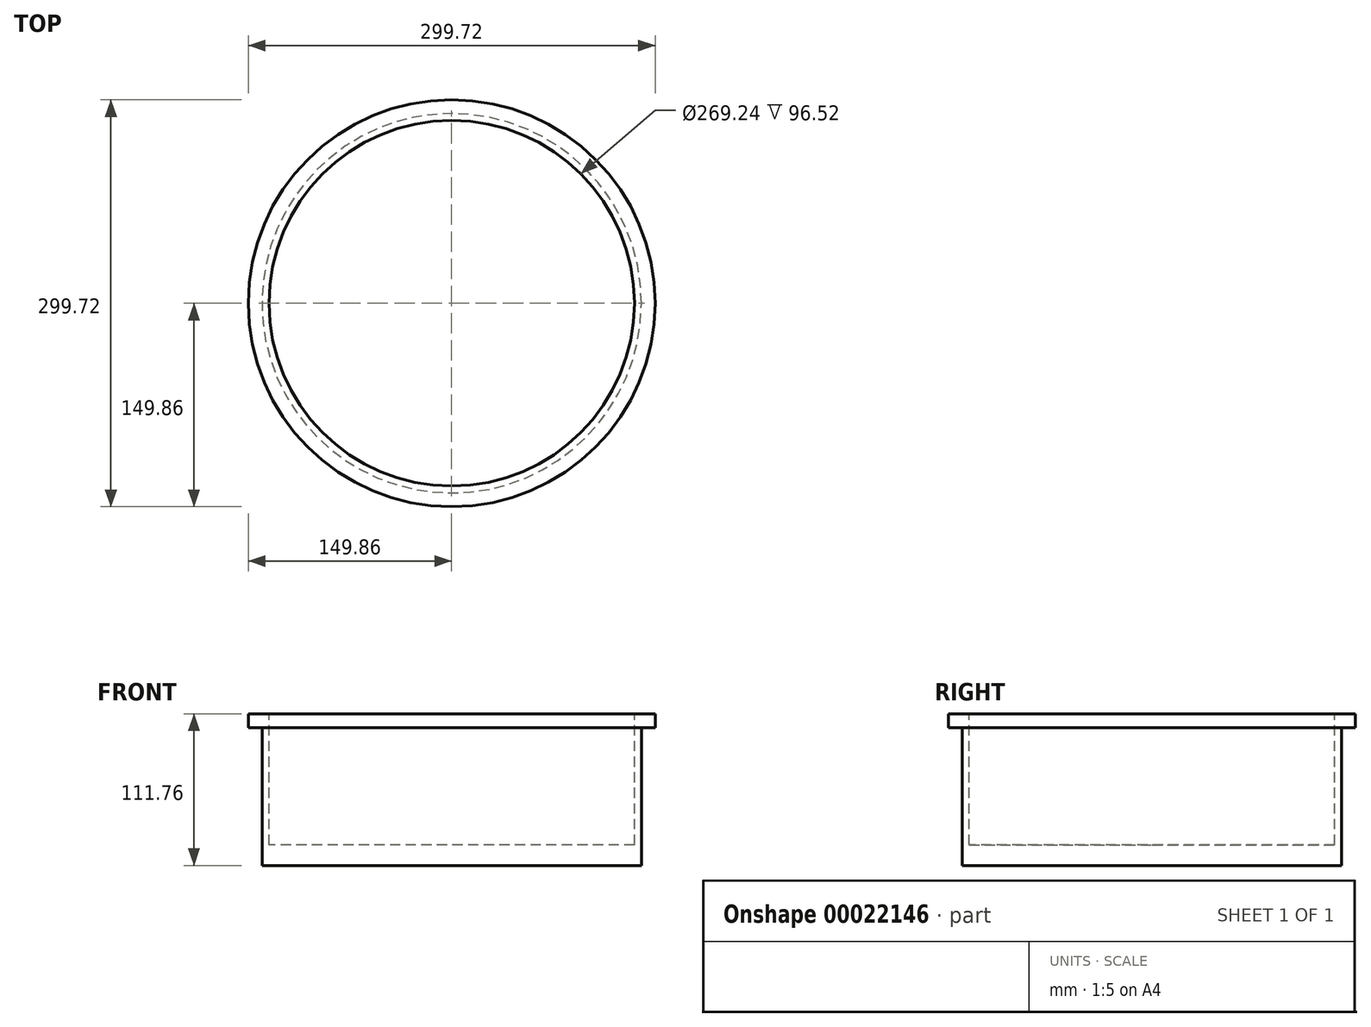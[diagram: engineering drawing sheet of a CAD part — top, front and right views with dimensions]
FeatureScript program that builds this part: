
annotation { "Feature Type Name" : "Feature", "Feature Type Description" : "" }
export const myFeature = defineFeature(function(context is Context, id is Id, definition is map)
    precondition{}
    {
        {
            var Q0;
            Q0=qCreatedBy(makeId("Front.planeOp"),FACE);
            var sketch = newSketch(context, id + "F0", { "sketchPlane" : qUnion([Q0])});
            skLineSegment(sketch, "E0.rect.bottom", {"start": v(149.86, 55.88) * mm, "end": v(0, 55.88) * mm});
            skLineSegment(sketch, "E0.rect.top", {"start": v(149.86, -55.88) * mm, "end": v(0, -55.88) * mm});
            skLineSegment(sketch, "E0.rect.left", {"start": v(149.86, 55.88) * mm, "end": v(149.86, -55.88) * mm});
            skPoint(sketch, "E0.rect.middle", {"position": v(0, 0) * mm});
            skPoint(sketch, "E1", {"position": v(0, 55.88) * mm});
            skPoint(sketch, "E2", {"position": v(0, -55.88) * mm});
            skLineSegment(sketch, "E3", {"start": v(0, 55.88) * mm, "end": v(0, -55.88) * mm});
            skPoint(sketch, "E0.rect.right.start.orphan", {"position": v(-149.86, 55.88) * mm});
            skPoint(sketch, "E4.orphan", {"position": v(-149.86, -55.88) * mm});
            skLineSegment(sketch, "E5", {"start": v(0, 75.72) * mm, "end": v(0, -77.55) * mm, "construction": true});
            skSolve(sketch);
        }
        {
            var Q0;
            Q0=makeQuery(id+"F0.imprint","IMPRINT",FACE,{"disambiguationData":[TD([[makeQuery(id+"F0.imprint","IMPRINT",EDGE,{"derivedFrom":sQuery(id+"F0.wireOp",EDGE,"E0.rect.bottom")}),1.0]])]});
            var Q1;
            Q1=sQuery(id+"F0.wireOp",EDGE,"E5");
            revolve(context, id + "F1", {"entities" : qUnion([Q0]), "axis" : qUnion([Q1]), "revolveType" : RevolveType.FULL});
        }
        {
            var Q0;
            Q0=makeQuery(id+"F1.opRevolve","SWEPT_FACE",FACE,{"disambiguationData":[OSD([sQuery(id+"F0.wireOp",EDGE,"E0.rect.top")])]});
            var sketch = newSketch(context, id + "F2", { "sketchPlane" : qUnion([Q0])});
            skCircle(sketch, "E6", {"center": v(0, 0) * mm, "radius": 139.7 * mm});
            skSolve(sketch);
        }
        {
            var Q0;
            Q0=makeQuery(id+"F2.imprint","IMPRINT",FACE,{"disambiguationData":[TD([[makeQuery(id+"F2.imprint","IMPRINT",EDGE,{"derivedFrom":sQuery(id+"F2.wireOp",EDGE,"E6")}),-1.0]])]});
            extrude(context, id + "F3", {"entities" : qUnion([Q0]), "operationType" : NewBodyOperationType.REMOVE, "oppositeDirection" : true, "depth" : 101.6 * mm});
        }
        {
            var Q0;
            Q0=makeQuery(id+"F1.opRevolve","SWEPT_FACE",FACE,{"disambiguationData":[OSD([sQuery(id+"F0.wireOp",EDGE,"E0.rect.bottom")])]});
            var sketch = newSketch(context, id + "F4", { "sketchPlane" : qUnion([Q0])});
            skCircle(sketch, "E7", {"center": v(0, 0) * mm, "radius": 134.62 * mm});
            skSolve(sketch);
        }
        {
            var Q0;
            Q0 = qSketchRegion(id + "F4", true);
            extrude(context, id + "F5", {"entities" : qUnion([Q0]), "operationType" : NewBodyOperationType.REMOVE, "oppositeDirection" : true, "depth" : 96.52 * mm});
        }
    });
